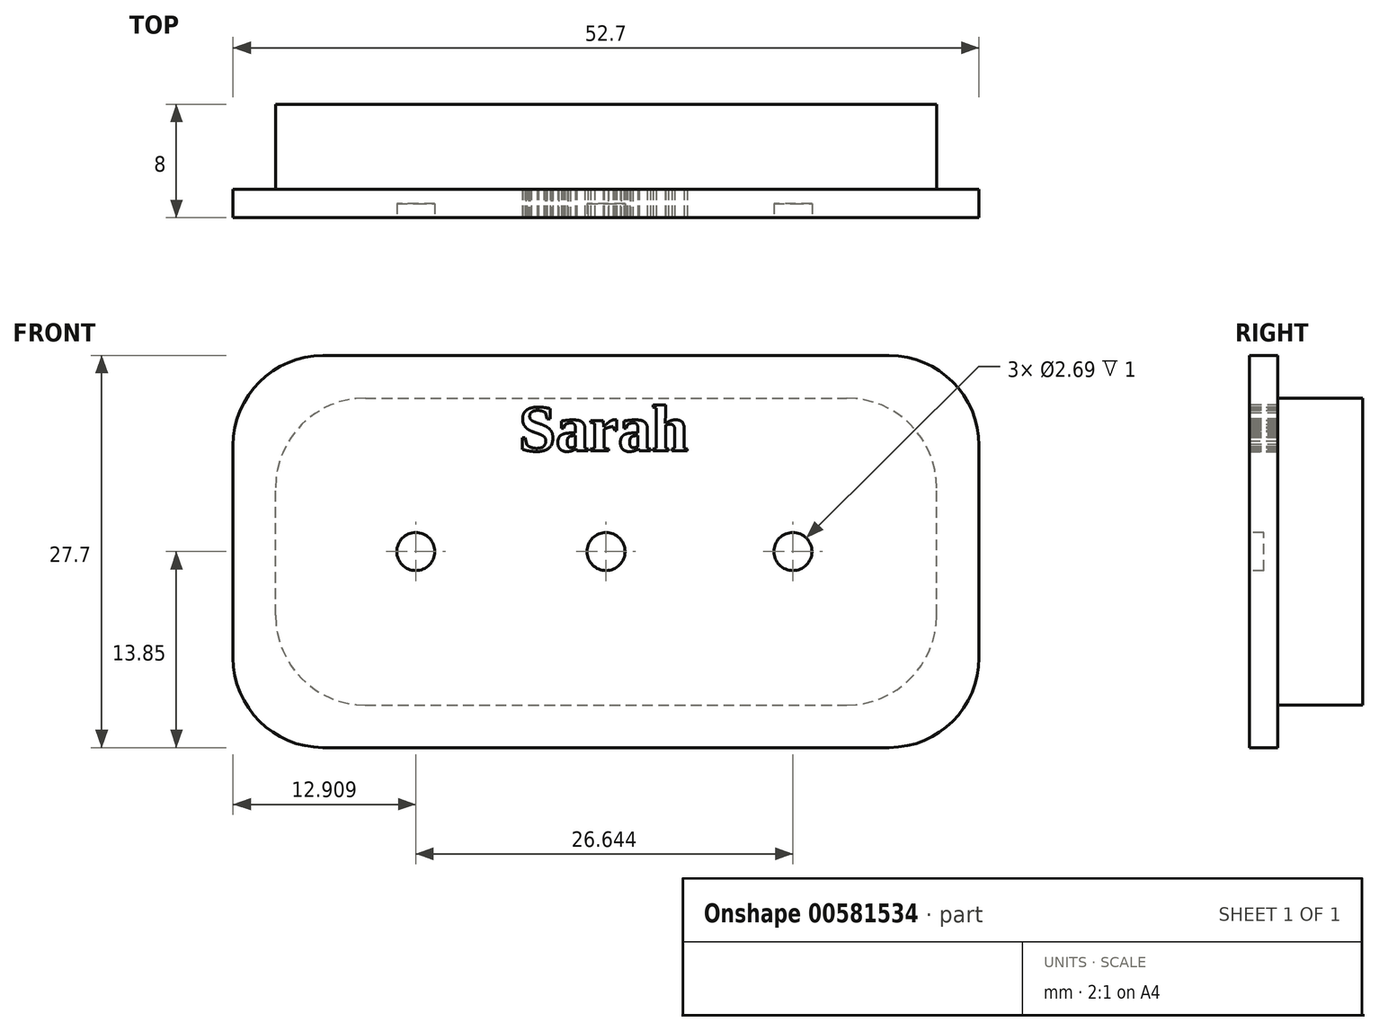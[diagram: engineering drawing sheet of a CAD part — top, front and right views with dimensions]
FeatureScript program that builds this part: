
annotation { "Feature Type Name" : "Feature", "Feature Type Description" : "" }
export const myFeature = defineFeature(function(context is Context, id is Id, definition is map)
    precondition{}
    {
        {
            var Q0;
            Q0=qCreatedBy(makeId("Front.planeOp"),FACE);
            var sketch = newSketch(context, id + "F0", { "sketchPlane" : qUnion([Q0])});
            skLineSegment(sketch, "E0.bottom", {"start": v(20, -13.85) * mm, "end": v(-20, -13.85) * mm});
            skLineSegment(sketch, "E0.top", {"start": v(20, 13.85) * mm, "end": v(-20, 13.85) * mm});
            skLineSegment(sketch, "E0.left", {"start": v(26.35, -7.5) * mm, "end": v(26.35, 7.5) * mm});
            skLineSegment(sketch, "E0.right", {"start": v(-26.35, -7.5) * mm, "end": v(-26.35, 7.5) * mm});
            skPoint(sketch, "E0.middle", {"position": v(0, 0) * mm});
            skPoint(sketch, "E1.visualSharp", {"position": v(-26.35, 13.85) * mm});
            skArc(sketch, "E1.filletArc", {"start": v(-20, 13.85) * mm, "mid": v(-24.5, 12) * mm, "end": v(-26.35, 7.5) * mm});
            skPoint(sketch, "E2.visualSharp", {"position": v(-26.35, -13.85) * mm});
            skArc(sketch, "E2.filletArc", {"start": v(-26.35, -7.5) * mm, "mid": v(-24.5, -12) * mm, "end": v(-20, -13.85) * mm});
            skPoint(sketch, "E3.visualSharp", {"position": v(26.35, 13.85) * mm});
            skArc(sketch, "E3.filletArc", {"start": v(26.35, 7.5) * mm, "mid": v(24.5, 12) * mm, "end": v(20, 13.85) * mm});
            skPoint(sketch, "E4.visualSharp", {"position": v(26.35, -13.85) * mm});
            skArc(sketch, "E4.filletArc", {"start": v(20, -13.85) * mm, "mid": v(24.5, -12) * mm, "end": v(26.35, -7.5) * mm});
            skSolve(sketch);
        }
        {
            var Q0;
            Q0=makeQuery(id+"F0.imprint","IMPRINT",FACE,{"disambiguationData":[TD([[makeQuery(id+"F0.imprint","IMPRINT",EDGE,{"derivedFrom":sQuery(id+"F0.wireOp",EDGE,"E0.bottom")}),-1.0]])]});
            extrude(context, id + "F1", {"entities" : qUnion([Q0]), "depth" : 2 * mm, "offsetDistance" : 25 * mm});
        }
        {
            var Q0;
            Q0=makeQuery(id+"F1.opExtrude","CAP_FACE",FACE,{"disambiguationData":[OSD([sQuery(id+"F0.wireOp",EDGE,"E0.bottom"),sQuery(id+"F0.wireOp",EDGE,"E0.top"),sQuery(id+"F0.wireOp",EDGE,"E0.left"),sQuery(id+"F0.wireOp",EDGE,"E0.right"),sQuery(id+"F0.wireOp",EDGE,"E1.filletArc"),sQuery(id+"F0.wireOp",EDGE,"E2.filletArc"),sQuery(id+"F0.wireOp",EDGE,"E3.filletArc"),sQuery(id+"F0.wireOp",EDGE,"E4.filletArc")])],"isStart":false});
            var sketch = newSketch(context, id + "F2", { "sketchPlane" : qUnion([Q0])});
            skCircle(sketch, "E5", {"center": v(-13.44, 0) * mm, "radius": 1.34 * mm});
            skCircle(sketch, "E6", {"center": v(0, 0) * mm, "radius": 1.34 * mm});
            skCircle(sketch, "E7", {"center": v(13.2, 0) * mm, "radius": 1.34 * mm});
            skSolve(sketch);
        }
        {
            var Q0;
            Q0=makeQuery(id+"F2.imprint","IMPRINT",FACE,{"disambiguationData":[TD([[makeQuery(id+"F2.imprint","IMPRINT",EDGE,{"derivedFrom":sQuery(id+"F2.wireOp",EDGE,"E5")}),1.0]])]});
            var Q1;
            Q1=makeQuery(id+"F2.imprint","IMPRINT",FACE,{"disambiguationData":[TD([[makeQuery(id+"F2.imprint","IMPRINT",EDGE,{"derivedFrom":sQuery(id+"F2.wireOp",EDGE,"E6")}),1.0]])]});
            var Q2;
            Q2=makeQuery(id+"F2.imprint","IMPRINT",FACE,{"disambiguationData":[TD([[makeQuery(id+"F2.imprint","IMPRINT",EDGE,{"derivedFrom":sQuery(id+"F2.wireOp",EDGE,"E7")}),1.0]])]});
            extrude(context, id + "F3", {"entities" : qUnion([Q0, Q1, Q2]), "operationType" : NewBodyOperationType.REMOVE, "oppositeDirection" : true, "depth" : 1 * mm, "offsetDistance" : 25 * mm});
        }
        {
            var Q0;
            Q0=makeQuery(id+"F1.opExtrude","CAP_FACE",FACE,{"disambiguationData":[OSD([sQuery(id+"F0.wireOp",EDGE,"E0.bottom"),sQuery(id+"F0.wireOp",EDGE,"E0.top"),sQuery(id+"F0.wireOp",EDGE,"E0.left"),sQuery(id+"F0.wireOp",EDGE,"E0.right"),sQuery(id+"F0.wireOp",EDGE,"E1.filletArc"),sQuery(id+"F0.wireOp",EDGE,"E2.filletArc"),sQuery(id+"F0.wireOp",EDGE,"E3.filletArc"),sQuery(id+"F0.wireOp",EDGE,"E4.filletArc")])],"isStart":true});
            var sketch = newSketch(context, id + "F4", { "sketchPlane" : qUnion([Q0])});
            skLineSegment(sketch, "E8.bottom", {"start": v(17, -10.85) * mm, "end": v(-17, -10.85) * mm});
            skLineSegment(sketch, "E8.top", {"start": v(17, 10.85) * mm, "end": v(-17, 10.85) * mm});
            skLineSegment(sketch, "E8.left", {"start": v(23.35, -4.5) * mm, "end": v(23.35, 4.5) * mm});
            skLineSegment(sketch, "E8.right", {"start": v(-23.35, -4.5) * mm, "end": v(-23.35, 4.5) * mm});
            skPoint(sketch, "E8.middle", {"position": v(0, 0) * mm});
            skPoint(sketch, "E9.visualSharp", {"position": v(-23.35, 10.85) * mm});
            skArc(sketch, "E9.filletArc", {"start": v(-17, 10.85) * mm, "mid": v(-21.5, 9) * mm, "end": v(-23.35, 4.5) * mm});
            skPoint(sketch, "E10.visualSharp", {"position": v(-23.35, -10.85) * mm});
            skArc(sketch, "E10.filletArc", {"start": v(-23.35, -4.5) * mm, "mid": v(-21.5, -9) * mm, "end": v(-17, -10.85) * mm});
            skPoint(sketch, "E11.visualSharp", {"position": v(23.35, 10.85) * mm});
            skArc(sketch, "E11.filletArc", {"start": v(23.35, 4.5) * mm, "mid": v(21.5, 9) * mm, "end": v(17, 10.85) * mm});
            skPoint(sketch, "E12.visualSharp", {"position": v(23.35, -10.85) * mm});
            skArc(sketch, "E12.filletArc", {"start": v(17, -10.85) * mm, "mid": v(21.5, -9) * mm, "end": v(23.35, -4.5) * mm});
            skSolve(sketch);
        }
        {
            var Q0;
            Q0=makeQuery(id+"F4.imprint","IMPRINT",FACE,{"disambiguationData":[TD([[makeQuery(id+"F4.imprint","IMPRINT",EDGE,{"derivedFrom":sQuery(id+"F4.wireOp",EDGE,"E8.bottom")}),-1.0]])]});
            extrude(context, id + "F5", {"entities" : qUnion([Q0]), "operationType" : NewBodyOperationType.ADD, "depth" : 6 * mm, "offsetDistance" : 25 * mm});
        }
        {
            var Q0;
            Q0=makeQuery(id+"F2.imprint","IMPRINT",FACE,{"disambiguationData":[TD([[makeQuery(id+"F2.imprint","IMPRINT",EDGE,{"derivedFrom":sQuery(id+"F2.wireOp",EDGE,"E5")}),-1.0]])]});
            var sketch = newSketch(context, id + "F6", { "sketchPlane" : qUnion([Q0])});
            skText(sketch, "E13", { "text": "Sarah", "fontName": "Tinos-Bold.ttf"});
            const initialGuessF6  = {"E13": [-0.00616, 0.00711, 1, 0, 0.00337]};
            skSetInitialGuess(sketch, initialGuessF6);
            skSolve(sketch);
        }
        {
            var Q0;
            Q0 = qSketchRegion(id + "F6", true);
            extrude(context, id + "F7", {"entities" : qUnion([Q0]), "operationType" : NewBodyOperationType.REMOVE, "oppositeDirection" : true, "depth" : 2 * mm, "offsetDistance" : 25 * mm});
        }
    });
